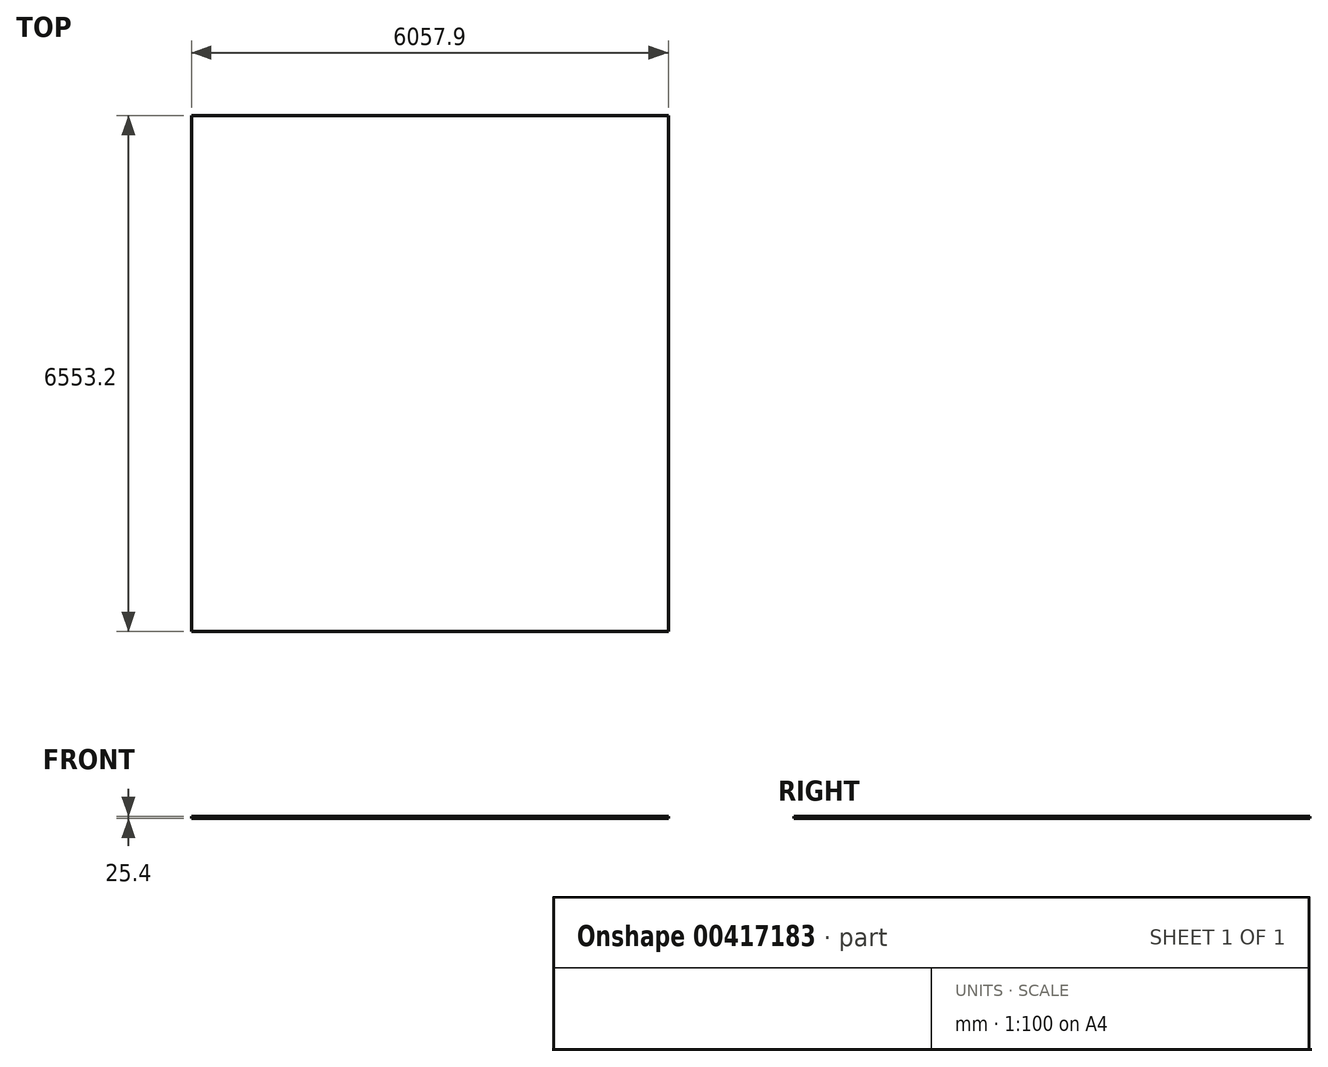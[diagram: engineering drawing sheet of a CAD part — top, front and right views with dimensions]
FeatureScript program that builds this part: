
annotation { "Feature Type Name" : "Feature", "Feature Type Description" : "" }
export const myFeature = defineFeature(function(context is Context, id is Id, definition is map)
    precondition{}
    {
        {
            var Q0;
            Q0=qCreatedBy(makeId("Top.planeOp"),FACE);
            var sketch = newSketch(context, id + "F0", { "sketchPlane" : qUnion([Q0])});
            skLineSegment(sketch, "E0.bottom", {"start": v(0, 0) * mm, "end": v(6057.9, 0) * mm});
            skLineSegment(sketch, "E0.top", {"start": v(0, 6553.2) * mm, "end": v(6057.9, 6553.2) * mm});
            skLineSegment(sketch, "E0.left", {"start": v(0, 0) * mm, "end": v(0, 6553.2) * mm});
            skLineSegment(sketch, "E0.right", {"start": v(6057.9, 0) * mm, "end": v(6057.9, 6553.2) * mm});
            skSolve(sketch);
        }
        {
            var Q0;
            Q0=makeQuery(id+"F0.imprint","IMPRINT",FACE,{"disambiguationData":[TD([[makeQuery(id+"F0.imprint","IMPRINT",EDGE,{"derivedFrom":sQuery(id+"F0.wireOp",EDGE,"E0.bottom")}),1.0]])]});
            extrude(context, id + "F1", {"entities" : qUnion([Q0]), "oppositeDirection" : true, "depth" : 25.4 * mm});
        }
    });
